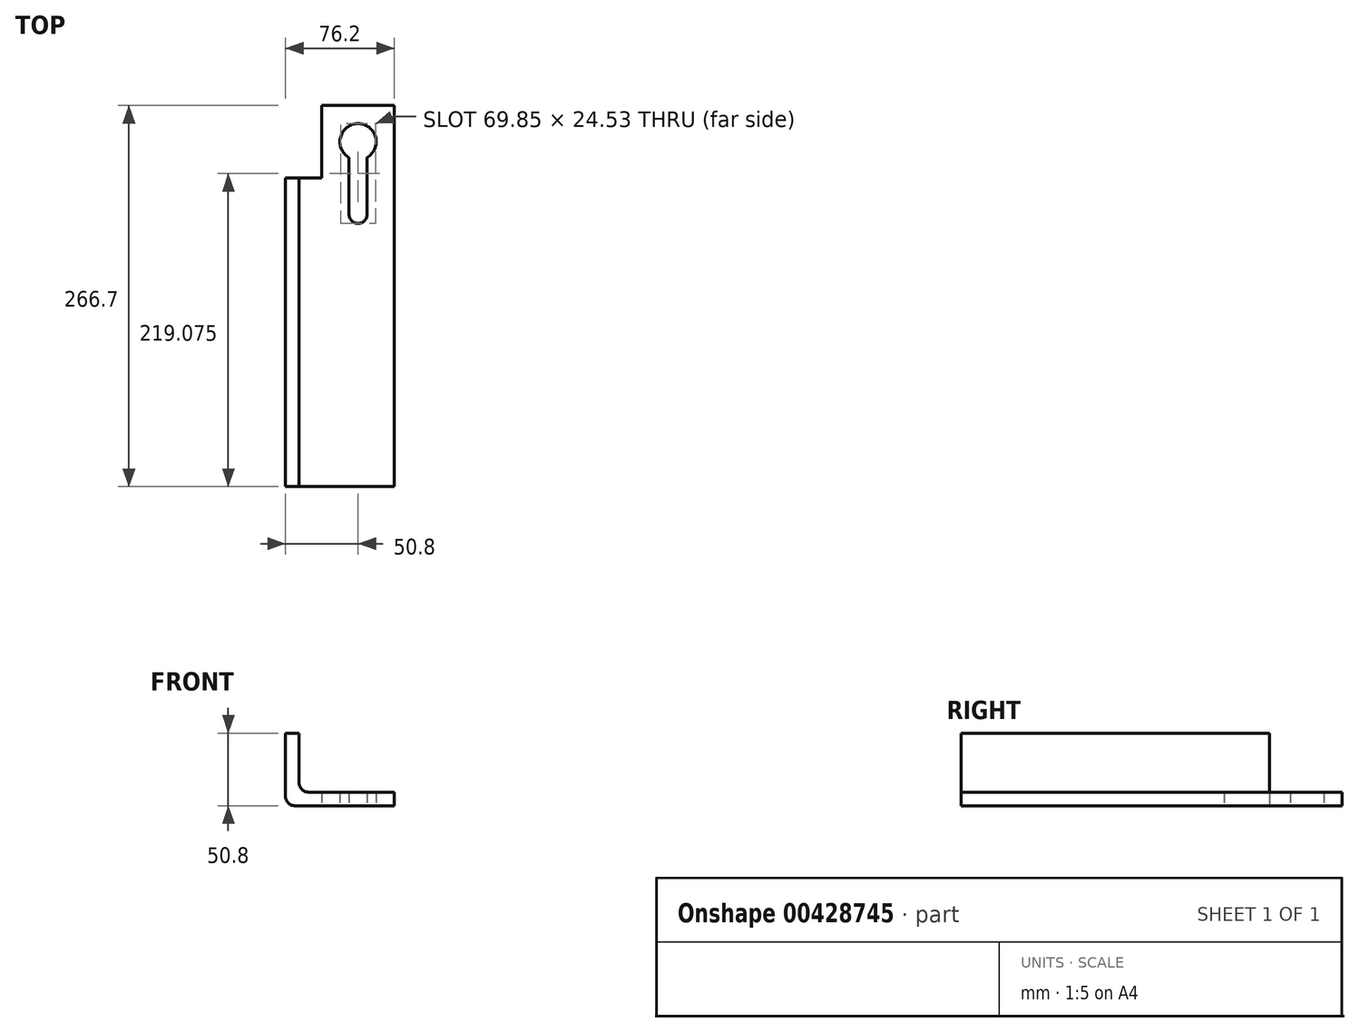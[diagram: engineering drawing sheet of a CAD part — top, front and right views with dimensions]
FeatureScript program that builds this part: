
annotation { "Feature Type Name" : "Feature", "Feature Type Description" : "" }
export const myFeature = defineFeature(function(context is Context, id is Id, definition is map)
    precondition{}
    {
        {
            var Q0;
            Q0=qCreatedBy(makeId("Front.planeOp"),FACE);
            var sketch = newSketch(context, id + "F0", { "sketchPlane" : qUnion([Q0])});
            skLineSegment(sketch, "E0", {"start": v(0, 50.8) * mm, "end": v(0, 6.35) * mm});
            skLineSegment(sketch, "E1", {"start": v(6.35, 0) * mm, "end": v(76.2, 0) * mm});
            skLineSegment(sketch, "E2", {"start": v(76.2, 0) * mm, "end": v(76.2, 9.53) * mm});
            skLineSegment(sketch, "E3", {"start": v(76.2, 9.53) * mm, "end": v(15.88, 9.53) * mm});
            skLineSegment(sketch, "E4", {"start": v(9.53, 15.88) * mm, "end": v(9.53, 50.8) * mm});
            skLineSegment(sketch, "E5", {"start": v(9.52, 50.8) * mm, "end": v(0, 50.8) * mm});
            skPoint(sketch, "E6.visualSharp", {"position": v(9.52, 9.53) * mm});
            skArc(sketch, "E6.filletArc", {"start": v(9.53, 15.88) * mm, "mid": v(11.38, 11.38) * mm, "end": v(15.88, 9.53) * mm});
            skPoint(sketch, "E7.visualSharp", {"position": v(0, 0) * mm});
            skArc(sketch, "E7.filletArc", {"start": v(0, 6.35) * mm, "mid": v(1.86, 1.86) * mm, "end": v(6.35, 0) * mm});
            skSolve(sketch);
        }
        {
            var Q0;
            Q0=makeQuery(id+"F0.imprint","IMPRINT",FACE,{"disambiguationData":[TD([[makeQuery(id+"F0.imprint","IMPRINT",EDGE,{"derivedFrom":sQuery(id+"F0.wireOp",EDGE,"E0")}),1.0]])]});
            extrude(context, id + "F1", {"entities" : qUnion([Q0]), "depth" : 215.9 * mm});
        }
        {
            var Q0;
            Q0=makeQuery(id+"F1.opExtrude","CAP_FACE",FACE,{"disambiguationData":[OSD([sQuery(id+"F0.wireOp",EDGE,"E0"),sQuery(id+"F0.wireOp",EDGE,"E1"),sQuery(id+"F0.wireOp",EDGE,"E2"),sQuery(id+"F0.wireOp",EDGE,"E3"),sQuery(id+"F0.wireOp",EDGE,"E4"),sQuery(id+"F0.wireOp",EDGE,"E5"),sQuery(id+"F0.wireOp",EDGE,"E6.filletArc"),sQuery(id+"F0.wireOp",EDGE,"E7.filletArc")])],"isStart":true});
            var sketch = newSketch(context, id + "F2", { "sketchPlane" : qUnion([Q0])});
            skLineSegment(sketch, "E8.bottom", {"start": v(-76.2, 9.53) * mm, "end": v(-25.4, 9.53) * mm});
            skLineSegment(sketch, "E8.top", {"start": v(-76.2, 0) * mm, "end": v(-25.4, 0) * mm});
            skLineSegment(sketch, "E8.left", {"start": v(-76.2, 9.53) * mm, "end": v(-76.2, 0) * mm});
            skLineSegment(sketch, "E8.right", {"start": v(-25.4, 9.53) * mm, "end": v(-25.4, 0) * mm});
            skSolve(sketch);
        }
        {
            var Q0;
            Q0=makeQuery(id+"F2.imprint","IMPRINT",FACE,{"disambiguationData":[TD([[makeQuery(id+"F2.imprint","IMPRINT",EDGE,{"derivedFrom":sQuery(id+"F2.wireOp",EDGE,"E8.bottom")}),-1.0]])]});
            extrude(context, id + "F3", {"entities" : qUnion([Q0]), "operationType" : NewBodyOperationType.ADD, "depth" : 50.8 * mm});
        }
        {
            var Q0;
            Q0=makeQuery(id+"F3.boolean.opBoolean","MERGE",FACE,{"derivedFrom":[makeQuery(id+"F1.opExtrude","SWEPT_FACE",FACE,{"disambiguationData":[OSD([sQuery(id+"F0.wireOp",EDGE,"E1")])]}),makeQuery(id+"F3.opExtrude","SWEPT_FACE",FACE,{"disambiguationData":[OSD([sQuery(id+"F2.wireOp",EDGE,"E8.top")])]})]});
            var sketch = newSketch(context, id + "F4", { "sketchPlane" : qUnion([Q0])});
            skLineSegment(sketch, "E9", {"start": v(44.45, -14.4) * mm, "end": v(44.45, 25.4) * mm});
            skLineSegment(sketch, "E10", {"start": v(57.15, 25.4) * mm, "end": v(57.15, -14.4) * mm});
            skArc(sketch, "E11", {"start": v(57.15, 25.4) * mm, "mid": v(50.8, 31.75) * mm, "end": v(44.45, 25.4) * mm});
            skArc(sketch, "E12", {"start": v(44.45, -14.4) * mm, "mid": v(50.8, -38.1) * mm, "end": v(57.15, -14.4) * mm});
            skSolve(sketch);
        }
        {
            var Q0;
            Q0=makeQuery(id+"F4.imprint","IMPRINT",FACE,{"disambiguationData":[TD([[makeQuery(id+"F4.imprint","IMPRINT",EDGE,{"derivedFrom":sQuery(id+"F4.wireOp",EDGE,"E9")}),-1.0]])]});
            extrude(context, id + "F5", {"entities" : qUnion([Q0]), "operationType" : NewBodyOperationType.REMOVE, "endBound" : BoundingType.THROUGH_ALL, "oppositeDirection" : true, "depth" : 25.4 * mm});
        }
    });
